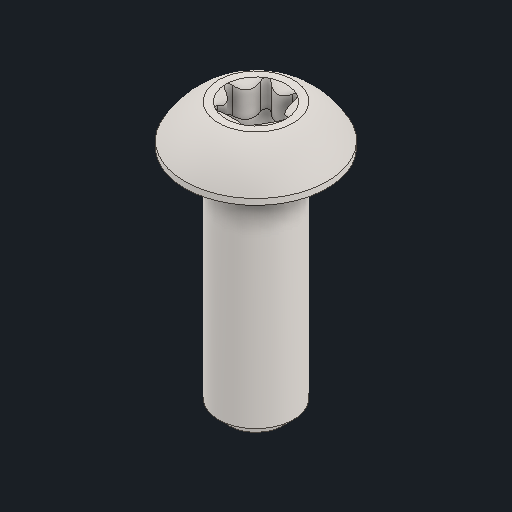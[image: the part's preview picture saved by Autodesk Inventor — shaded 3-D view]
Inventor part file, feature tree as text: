
AUTODESK INVENTOR PART (.ipt)
format: ipt  version: 2024 (Build 280153000, 153)  size: 178,176 bytes
history: native  units: in
note: dims shown in document units (in); Inventor stores cm internally (conversion verified against a paired STEP export)
features: chamfer x1
ambient origin geometry x8: Origin, YZ Plane, XZ Plane, XY Plane, X Axis, Y Axis, Z Axis, Center Point
bodies: Solid1 (feature_tree)
feature tree (1):
  chamfer  "Chamfer2"  [1 undecoded]
note: 1 required parameter value undecoded (feature->parameter linkage not recoverable at this tier; creation-order binding heuristic only, values carry confidence <= 0.55)
